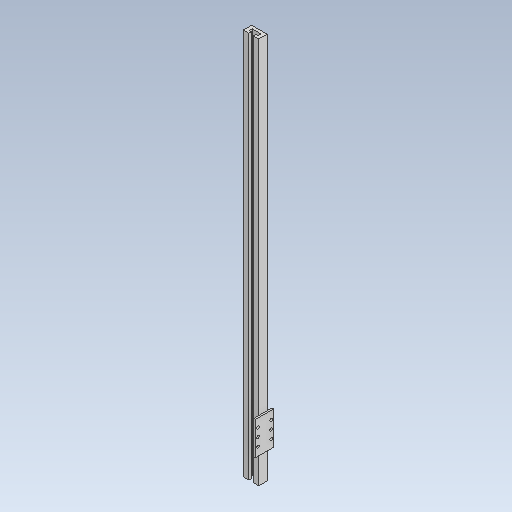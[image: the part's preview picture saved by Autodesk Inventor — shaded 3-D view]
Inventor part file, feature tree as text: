
AUTODESK INVENTOR PART (.ipt)
format: ipt  version: 2021 (Build 250183000, 183)  size: 140,288 bytes
history: native  units: in
note: dims shown in document units (in); Inventor stores cm internally (conversion verified against a paired STEP export)
features: sketch x5, other x3, thicken_offset x2
ambient origin geometry x8: Origin, YZ Plane, XZ Plane, XY Plane, X Axis, Y Axis, Z Axis, Center Point
bodies: Solid1 (feature_tree)
feature tree (10):
  other  "Rail.ipt"
  thicken_offset  "Thicken1"
  thicken_offset  "Thicken2"
  other  "Solid1::Rail.ipt"
  other  "TaggingFeature1"
  sketch  "Sketch1"  dims[d0=0.3937in]
  sketch  "Sketch2"  dims[d1=7.874in]
  sketch  "Sketch3"  dims[d2=7.874in]
  sketch  "Sketch4"  dims[d3=7.874in]
  sketch  "Sketch5"  dims[d4=7.874in]
